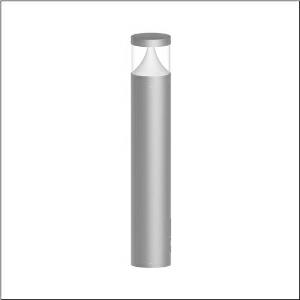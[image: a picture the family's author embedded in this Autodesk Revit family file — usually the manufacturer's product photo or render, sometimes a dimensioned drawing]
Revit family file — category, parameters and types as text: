
# Revit family: cl_31_poller_90_5cl444603
name_source: partatom
category: Lighting Fixtures
units: mm (PartAtom-declared; Revit-internal decimal feet)

## family parameters
Cut with Voids When Loaded = No
Host = Face
Light Source = No
Part Type = Normal
Room Calculation Point = No
Round Connector Dimension = Use Diameter
Shared = No

## types (1)
- --- (1 x LED, 1500 lm, 14 W, 3000K)
    Apparent Load = 14 VA
    CIE Flux Codes = 19 66 88 92 100
    Color Rendering = 80
    Color Temperature = 3000K
    Default Elevation = 1800 mm
    Description = CL 31 Bollard 90, bollard luminaire, primary light control with lens, of PC, primary optical cover: cover panel, of PC, transparent, secondary light control with reflector, of PC, primary light characteristic: asymmetric, LED, rated luminous flux: 1.500lm, luminous efficacy: 107lm/W, light colour: 830, colour temperature: 3000K, control gear: DALI, with terminal, 5-pole, max. 2.5mm², mains connection: 220..240V, AC, 50/60Hz, rated input power: 14W, luminaire housing, of aluminium, powder-coated, Siteco® metallic grey, diameter: 170mm, height: 900mm, protection rating (complete): IP65, insulation class (complete): insulation class I (protective earthing), certification: CE, ENEC, impact resistance: IK10, permissible operating ambient temperature for outdoor applications: -20..+50°C, packaging unit: 1 piece
    Height = 200 mm  [stored 0.656168 ft]
    Lamp = 1 x LED
    Lamp Light Flux = 1500 lm
    Lamp Power = 14 W
    Lamp count = 1
    Length = 170 mm  [stored 0.557743 ft]
    Luminous efficacy = 107 lm/W
    Manufacturer = Siteco
    ModVariant = No
    Model = 5CL444603
    Mounting Place = Floor
    Mounting Type = Freestanding
    Number of Poles = 1
    OnlyDefault = Yes
    Power Factor = 1
    Product Name = CL 31 Poller 90
    Product group = bollard luminaire
    ProductGroupID = 1304
    Protection Class = Protection class I
    Protection Degree = IP 65
    RLX_Detail_Level = 1
    RLX_Emergency_Light_Flux = 0 lm
    RLX_Emergency_Type = 0
    RLX_Emergency_Type_DB = No
    RlxData = <blob elided: 65473 chars, md5=56707a5a>
    Socket = socket
    Standby Power = 0 W
    System Light Flux = 1500 lm
    System Power = 14 W
    Type Comments = factory setting: luminous flux: 100 % | dim-lin: 254 | 350 mA
    Type Image = l_1006899.jpg
    URL = http://relux.com
    VarID = @adj_195234
    Voltage = 0 V
    Weight = 0.00 kg
    Width = 0 mm  [stored 0 ft]

note: [stored X ft] marks values corroborated as IEEE doubles in the binary element streams (Revit-internal decimal feet)

## geometry (parser evidence)
native form markers: Blend x4, Sweep x12
no freeform markers — native parametric forms only
